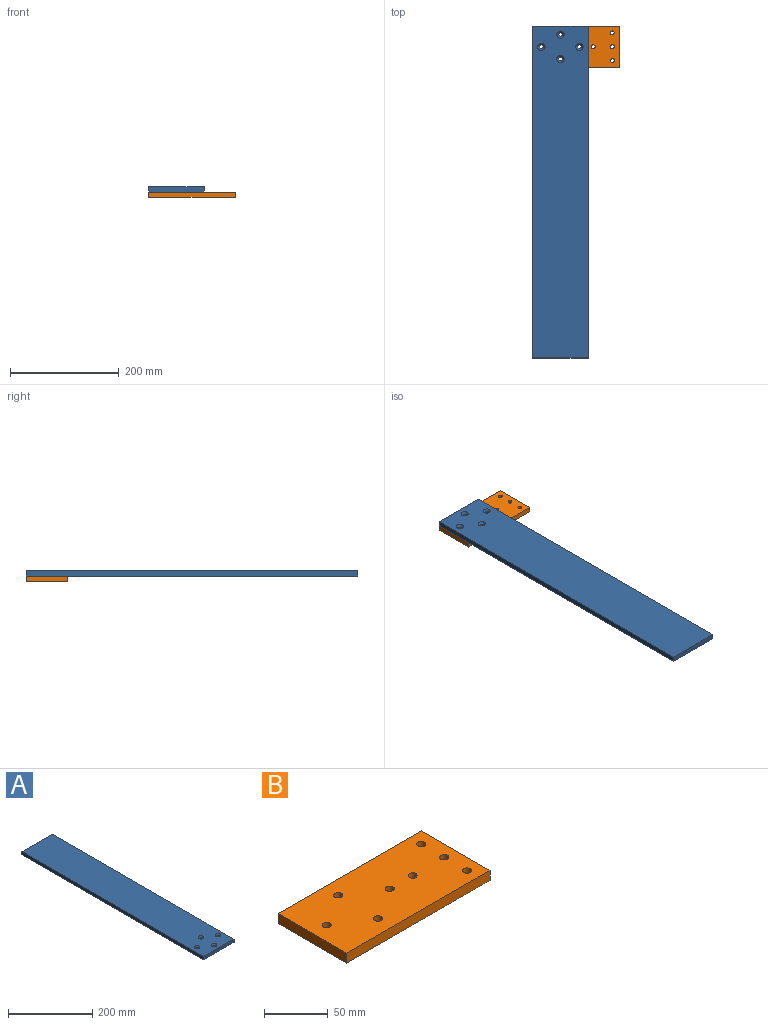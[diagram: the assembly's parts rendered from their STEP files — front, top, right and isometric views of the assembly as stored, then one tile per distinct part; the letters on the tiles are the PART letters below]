
ASSEMBLY  parts=2 mates=1
PART A: 14 faces, bbox 101.6x609.6x9.5 mm
  f0: plane 101.6x9.53mm, normal (0,1,0), area 967.7mm2, adj f1,f3,f4,f5
  f1: plane 609.6x9.53mm, normal (-1,0,0), area 5806.4mm2, adj f0,f2,f4,f5
  f2: plane 101.6x9.53mm, normal (0,-1,0), area 967.7mm2, adj f1,f3,f4,f5
  f3: plane 609.6x9.53mm, normal (1,0,0), area 5806.4mm2, adj f0,f2,f4,f5
  f4: plane 609.6x101.6mm, normal (0,0,-1), area 61775.3mm2, adj f0,f1,f2,f3,f6,f8,f10,f12
  f5: plane 609.6x101.6mm, normal (0,0,1), area 61363.9mm2, adj f0,f1,f2,f3,f7,f9,f11,f13
  f6: cylinder r=3.57mm len=7.14mm, axis (0,0,1), area 131.7mm2, adj f4,f7
  f7: cone r=3.57mm half-angle=41deg, axis (0,0,1), area 156.8mm2, adj f5,f6
  f8: cylinder r=3.57mm len=7.14mm, axis (0,0,1), area 131.7mm2, adj f4,f9
  f9: cone r=3.57mm half-angle=41deg, axis (0,0,1), area 156.8mm2, adj f5,f8
  f10: cylinder r=3.57mm len=7.14mm, axis (0,0,1), area 131.7mm2, adj f4,f11
  f11: cone r=3.57mm half-angle=41deg, axis (0,0,1), area 156.8mm2, adj f5,f10
  f12: cylinder r=3.57mm len=7.14mm, axis (0,0,1), area 131.7mm2, adj f4,f13
  f13: cone r=3.57mm half-angle=41deg, axis (0,0,1), area 156.8mm2, adj f5,f12
PART B: 14 faces, bbox 158.8x76.2x9.5 mm
  f0: plane 158.75x9.53mm, normal (0,1,0), area 1512.1mm2, adj f1,f3,f4,f5
  f1: plane 76.2x9.53mm, normal (-1,0,0), area 725.8mm2, adj f0,f2,f4,f5
  f2: plane 158.75x9.53mm, normal (0,-1,0), area 1512.1mm2, adj f1,f3,f4,f5
  f3: plane 76.2x9.53mm, normal (1,0,0), area 725.8mm2, adj f0,f2,f4,f5
  f4: plane 158.75x76.2mm, normal (0,0,1), area 11776.7mm2, adj f0,f1,f2,f3,f6,f7,f8,f9
  f5: plane 158.75x76.2mm, normal (0,0,-1), area 11776.7mm2, adj f0,f1,f2,f3,f6,f7,f8,f9
  f6: cylinder r=3.57mm len=9.53mm, axis (0,0,-1), area 213.6mm2, adj f4,f5
  f7: cylinder r=3.57mm len=9.53mm, axis (0,0,-1), area 213.6mm2, adj f4,f5
  f8: cylinder r=3.57mm len=9.53mm, axis (0,0,-1), area 213.6mm2, adj f4,f5
  f9: cylinder r=3.57mm len=9.53mm, axis (0,0,-1), area 213.6mm2, adj f4,f5
  f10: cylinder r=3.57mm len=9.53mm, axis (0,0,-1), area 213.6mm2, adj f4,f5
  f11: cylinder r=3.57mm len=9.53mm, axis (0,0,-1), area 213.6mm2, adj f4,f5
  f12: cylinder r=3.57mm len=9.53mm, axis (0,0,-1), area 213.6mm2, adj f4,f5
  f13: cylinder r=3.57mm len=9.53mm, axis (0,0,-1), area 213.6mm2, adj f4,f5
PLACE A rot(axis=(0,0,1),180deg) t=(-13.12,-255.25,18.08)mm
PLACE B t=(15.45,11.45,-0.97)mm
MATE fastened A.f6 <-> B.f11  axis (0,0,-1) through (-13.12,33.67,8.55)mm
